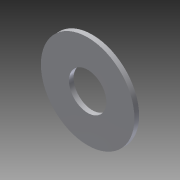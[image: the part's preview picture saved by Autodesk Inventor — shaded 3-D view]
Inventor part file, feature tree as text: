
AUTODESK INVENTOR PART (.ipt)
format: ipt  version: 2013 (Build 170138000, 138)  size: 77,312 bytes
history: native  units: mm
features: other x1, extrude x1, sketch x1
ambient origin geometry x8: Origin, YZ Plane, XZ Plane, XY Plane, X Axis, Y Axis, Z Axis, Center Point
feature tree (3):
  other  "ソリッド1"
  extrude  "押し出し1"  Depth=20.0mm
  sketch  "スケッチ1"
